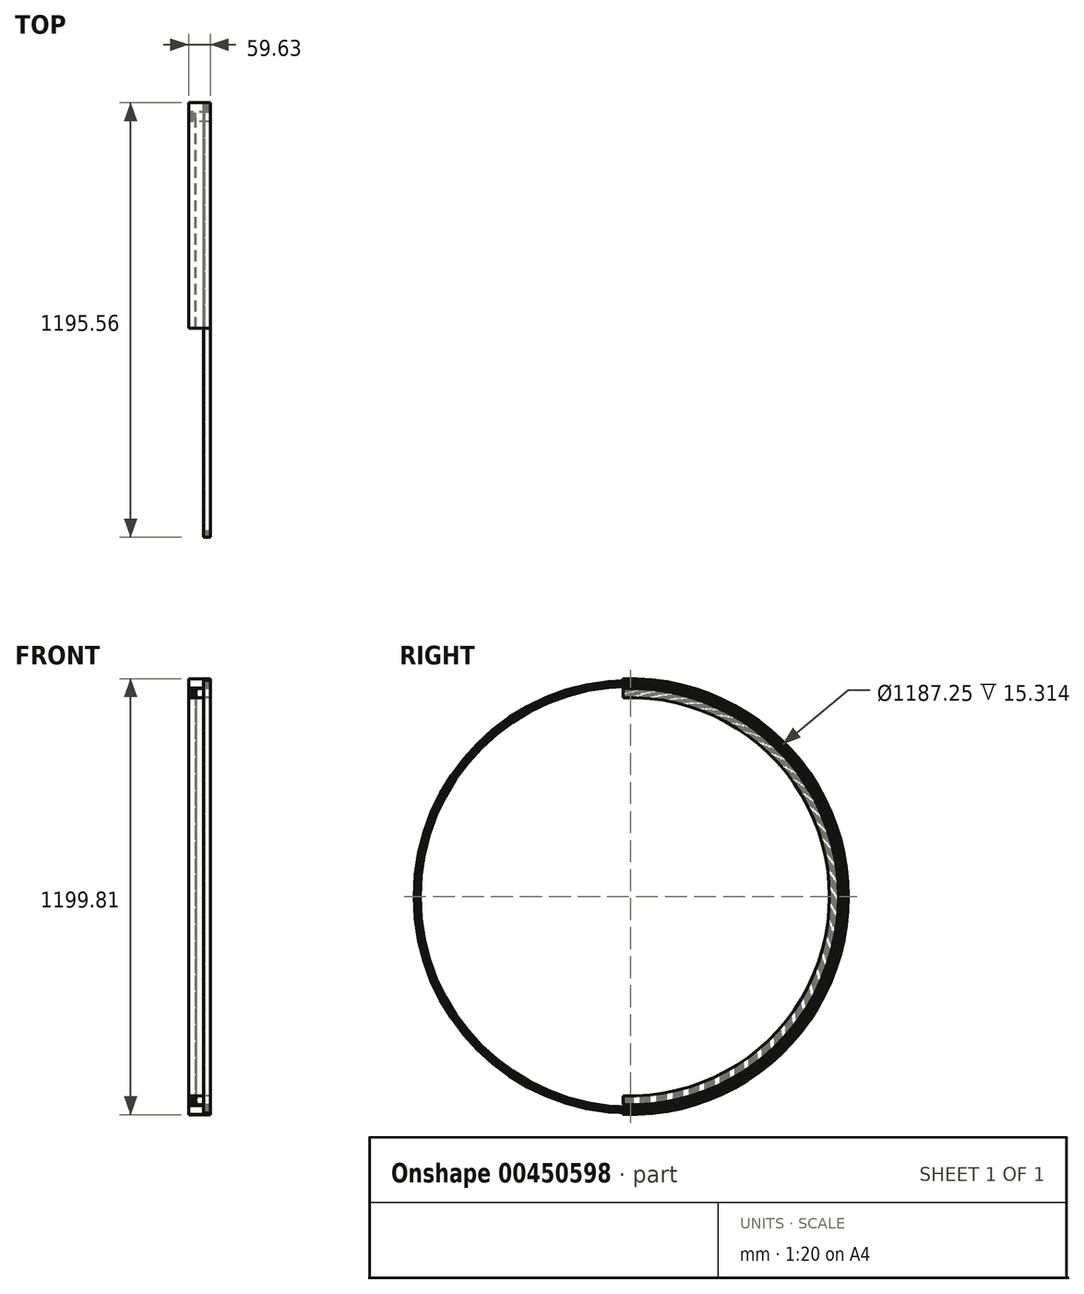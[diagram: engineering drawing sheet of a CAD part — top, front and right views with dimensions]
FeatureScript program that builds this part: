
annotation { "Feature Type Name" : "Feature", "Feature Type Description" : "" }
export const myFeature = defineFeature(function(context is Context, id is Id, definition is map)
    precondition{}
    {
        {
            var Q0;
            Q0=qCreatedBy(makeId("Front.planeOp"),FACE);
            var sketch = newSketch(context, id + "F0", { "sketchPlane" : qUnion([Q0])});
            skLineSegment(sketch, "E0", {"start": v(-20.96, 26.89) * mm, "end": v(38.1, 26.89) * mm});
            skLineSegment(sketch, "E1", {"start": v(38.1, 26.89) * mm, "end": v(38.1, 2.12) * mm});
            skLineSegment(sketch, "E2", {"start": v(38.1, 2.12) * mm, "end": v(-20.53, 2.12) * mm});
            skLineSegment(sketch, "E3", {"start": v(-20.53, 2.12) * mm, "end": v(-20.53, 5.72) * mm});
            skLineSegment(sketch, "E4", {"start": v(-20.53, 5.72) * mm, "end": v(0, 5.72) * mm});
            skLineSegment(sketch, "E5", {"start": v(0, 5.72) * mm, "end": v(0, 12.49) * mm});
            skLineSegment(sketch, "E6", {"start": v(0, 12.49) * mm, "end": v(-20.74, 12.49) * mm});
            skLineSegment(sketch, "E7", {"start": v(-20.74, 12.49) * mm, "end": v(-20.74, 16.09) * mm});
            skLineSegment(sketch, "E8", {"start": v(-20.74, 16.09) * mm, "end": v(0, 16.09) * mm});
            skLineSegment(sketch, "E9", {"start": v(0, 16.09) * mm, "end": v(0, 23.07) * mm});
            skLineSegment(sketch, "E10", {"start": v(0, 23.07) * mm, "end": v(-20.96, 23.07) * mm});
            skLineSegment(sketch, "E11", {"start": v(-20.96, 23.07) * mm, "end": v(-20.96, 26.89) * mm});
            skSolve(sketch);
        }
        {
            var Q0;
            Q0=qCreatedBy(makeId("Front.planeOp"),FACE);
            var sketch = newSketch(context, id + "F1", { "sketchPlane" : qUnion([Q0])});
            skLineSegment(sketch, "E12", {"start": v(-719.26, 575.27) * mm, "end": v(839.78, 575.27) * mm, "construction": true});
            skSolve(sketch);
        }
        {
            var Q0;
            Q0=qCreatedBy(makeId("Front.planeOp"),FACE);
            var sketch = newSketch(context, id + "F2", { "sketchPlane" : qUnion([Q0])});
            skLineSegment(sketch, "E13", {"start": v(-20.65, 22.58) * mm, "end": v(-0.65, 22.58) * mm});
            skLineSegment(sketch, "E14", {"start": v(-0.65, 22.58) * mm, "end": v(-0.65, 16.61) * mm});
            skLineSegment(sketch, "E15", {"start": v(-0.65, 16.61) * mm, "end": v(-20.65, 16.61) * mm});
            skLineSegment(sketch, "E16", {"start": v(-20.65, 16.61) * mm, "end": v(-20.65, 18.64) * mm});
            skLineSegment(sketch, "E17", {"start": v(-20.65, 18.64) * mm, "end": v(-2.76, 18.64) * mm});
            skLineSegment(sketch, "E18", {"start": v(-2.76, 18.64) * mm, "end": v(-2.76, 20.17) * mm});
            skLineSegment(sketch, "E19", {"start": v(-2.76, 20.17) * mm, "end": v(-20.65, 20.17) * mm});
            skLineSegment(sketch, "E20", {"start": v(-20.65, 20.17) * mm, "end": v(-20.65, 22.58) * mm});
            skLineSegment(sketch, "E21", {"start": v(-20.65, 12.03) * mm, "end": v(-0.65, 12.03) * mm});
            skLineSegment(sketch, "E22", {"start": v(-0.65, 12.03) * mm, "end": v(-0.65, 6.07) * mm});
            skLineSegment(sketch, "E23", {"start": v(-0.65, 6.07) * mm, "end": v(-20.65, 6.07) * mm});
            skLineSegment(sketch, "E24", {"start": v(-20.65, 6.07) * mm, "end": v(-20.65, 8.1) * mm});
            skLineSegment(sketch, "E25", {"start": v(-20.65, 8.1) * mm, "end": v(-2.76, 8.1) * mm});
            skLineSegment(sketch, "E26", {"start": v(-2.76, 8.1) * mm, "end": v(-2.76, 9.62) * mm});
            skLineSegment(sketch, "E27", {"start": v(-2.76, 9.62) * mm, "end": v(-20.65, 9.62) * mm});
            skLineSegment(sketch, "E28", {"start": v(-20.65, 9.62) * mm, "end": v(-20.65, 12.03) * mm});
            skSolve(sketch);
        }
        {
            var Q0;
            Q0 = qSketchRegion(id + "F0", true);
            var Q1;
            Q1=sQuery(id+"F1.wireOp",EDGE,"E12");
            revolve(context, id + "F3", {"entities" : qUnion([Q0]), "axis" : qUnion([Q1]), "revolveType" : RevolveType.FULL});
        }
        {
            var Q0;
            Q0 = qSketchRegion(id + "F2", true);
            var Q1;
            Q1=sQuery(id+"F1.wireOp",EDGE,"E12");
            revolve(context, id + "F4", {"entities" : qUnion([Q0]), "axis" : qUnion([Q1]), "revolveType" : RevolveType.FULL});
        }
        {
            var Q0;
            Q0=qCreatedBy(makeId("Right.planeOp"),FACE);
            var sketch = newSketch(context, id + "F5", { "sketchPlane" : qUnion([Q0])});
            skLineSegment(sketch, "E29.bottom", {"start": v(-20.41, -23.47) * mm, "end": v(-612.3, -23.47) * mm});
            skLineSegment(sketch, "E29.top", {"start": v(-20.41, 1163.72) * mm, "end": v(-612.3, 1163.72) * mm});
            skLineSegment(sketch, "E29.left", {"start": v(-20.41, -23.47) * mm, "end": v(-20.41, 1163.72) * mm});
            skLineSegment(sketch, "E29.right", {"start": v(-612.3, -23.47) * mm, "end": v(-612.3, 1163.72) * mm});
            skSolve(sketch);
        }
        {
            var Q0;
            Q0 = qSketchRegion(id + "F5", true);
            extrude(context, id + "F6", {"entities" : qUnion([Q0]), "operationType" : NewBodyOperationType.REMOVE, "endBound" : BoundingType.SYMMETRIC, "oppositeDirection" : true, "depth" : 254 * mm});
        }
        {
            var Q0;
            Q0=qCreatedBy(makeId("Front.planeOp"),FACE);
            var sketch = newSketch(context, id + "F7", { "sketchPlane" : qUnion([Q0])});
            skLineSegment(sketch, "E30", {"start": v(-20.23, 0.13) * mm, "end": v(38.32, 0.13) * mm});
            skLineSegment(sketch, "E31", {"start": v(-20.23, 0.13) * mm, "end": v(-20.23, -24.64) * mm});
            skLineSegment(sketch, "E32", {"start": v(38.67, -24.64) * mm, "end": v(-20.23, -24.64) * mm});
            skLineSegment(sketch, "E33", {"start": v(38.67, -24.64) * mm, "end": v(38.67, -21.04) * mm});
            skLineSegment(sketch, "E34", {"start": v(19.63, -21.04) * mm, "end": v(38.67, -21.04) * mm});
            skLineSegment(sketch, "E35", {"start": v(19.63, -21.04) * mm, "end": v(19.63, -14.27) * mm});
            skLineSegment(sketch, "E36", {"start": v(38.29, -14.27) * mm, "end": v(19.63, -14.27) * mm});
            skLineSegment(sketch, "E37", {"start": v(38.29, -14.27) * mm, "end": v(38.29, -10.67) * mm});
            skLineSegment(sketch, "E38", {"start": v(19.46, -10.67) * mm, "end": v(38.29, -10.67) * mm});
            skLineSegment(sketch, "E39", {"start": v(19.46, -10.67) * mm, "end": v(19.46, -3.68) * mm});
            skLineSegment(sketch, "E40", {"start": v(38.32, -3.68) * mm, "end": v(19.46, -3.68) * mm});
            skLineSegment(sketch, "E41", {"start": v(38.32, -3.68) * mm, "end": v(38.32, 0.13) * mm});
            skSolve(sketch);
        }
        {
            var Q0;
            Q0 = qSketchRegion(id + "F7", true);
            var Q1;
            Q1=sQuery(id+"F1.wireOp",EDGE,"E12");
            revolve(context, id + "F8", {"entities" : qUnion([Q0]), "axis" : qUnion([Q1]), "revolveType" : RevolveType.FULL});
        }
        {
            var Q0;
            Q0=qCreatedBy(makeId("Right.planeOp"),FACE);
            var sketch = newSketch(context, id + "F9", { "sketchPlane" : qUnion([Q0])});
            skLineSegment(sketch, "E42.bottom", {"start": v(-21.16, -26.22) * mm, "end": v(-755.12, -26.22) * mm});
            skLineSegment(sketch, "E42.top", {"start": v(-21.16, 1216.27) * mm, "end": v(-755.12, 1216.27) * mm});
            skLineSegment(sketch, "E42.left", {"start": v(-21.16, -26.22) * mm, "end": v(-21.16, 1216.27) * mm});
            skLineSegment(sketch, "E42.right", {"start": v(-755.12, -26.22) * mm, "end": v(-755.12, 1216.27) * mm});
            skSolve(sketch);
        }
        {
            var Q0;
            Q0 = qSketchRegion(id + "F9", true);
            extrude(context, id + "F10", {"entities" : qUnion([Q0]), "operationType" : NewBodyOperationType.REMOVE, "endBound" : BoundingType.SYMMETRIC, "oppositeDirection" : true, "depth" : 152.4 * mm});
        }
        {
            var Q0;
            Q0=qCreatedBy(makeId("Front.planeOp"),FACE);
            var sketch = newSketch(context, id + "F11", { "sketchPlane" : qUnion([Q0])});
            skLineSegment(sketch, "E43", {"start": v(20.18, -3.88) * mm, "end": v(38.36, -3.88) * mm});
            skLineSegment(sketch, "E44", {"start": v(20.18, -3.88) * mm, "end": v(20.18, -9.85) * mm});
            skLineSegment(sketch, "E45", {"start": v(38.34, -9.85) * mm, "end": v(20.18, -9.85) * mm});
            skLineSegment(sketch, "E46", {"start": v(38.34, -9.85) * mm, "end": v(38.34, -7.81) * mm});
            skLineSegment(sketch, "E47", {"start": v(23.05, -7.81) * mm, "end": v(38.34, -7.81) * mm});
            skLineSegment(sketch, "E48", {"start": v(23.05, -7.81) * mm, "end": v(23.05, -6.3) * mm});
            skLineSegment(sketch, "E49", {"start": v(38.36, -6.3) * mm, "end": v(23.05, -6.3) * mm});
            skLineSegment(sketch, "E50", {"start": v(38.36, -6.3) * mm, "end": v(38.36, -3.88) * mm});
            skLineSegment(sketch, "E51", {"start": v(20.18, -14.43) * mm, "end": v(38.34, -14.43) * mm});
            skLineSegment(sketch, "E52", {"start": v(20.18, -14.43) * mm, "end": v(20.18, -20.4) * mm});
            skLineSegment(sketch, "E53", {"start": v(38.36, -20.4) * mm, "end": v(20.18, -20.4) * mm});
            skLineSegment(sketch, "E54", {"start": v(38.36, -20.4) * mm, "end": v(38.36, -18.36) * mm});
            skLineSegment(sketch, "E55", {"start": v(23.05, -18.36) * mm, "end": v(38.36, -18.36) * mm});
            skLineSegment(sketch, "E56", {"start": v(23.05, -18.36) * mm, "end": v(23.05, -16.84) * mm});
            skLineSegment(sketch, "E57", {"start": v(38.34, -16.84) * mm, "end": v(23.05, -16.84) * mm});
            skLineSegment(sketch, "E58", {"start": v(38.34, -16.84) * mm, "end": v(38.34, -14.43) * mm});
            skSolve(sketch);
        }
        {
            var Q0;
            Q0 = qSketchRegion(id + "F11", true);
            var Q1;
            Q1=sQuery(id+"F1.wireOp",EDGE,"E12");
            revolve(context, id + "F12", {"entities" : qUnion([Q0]), "axis" : qUnion([Q1]), "revolveType" : RevolveType.FULL});
        }
    });
